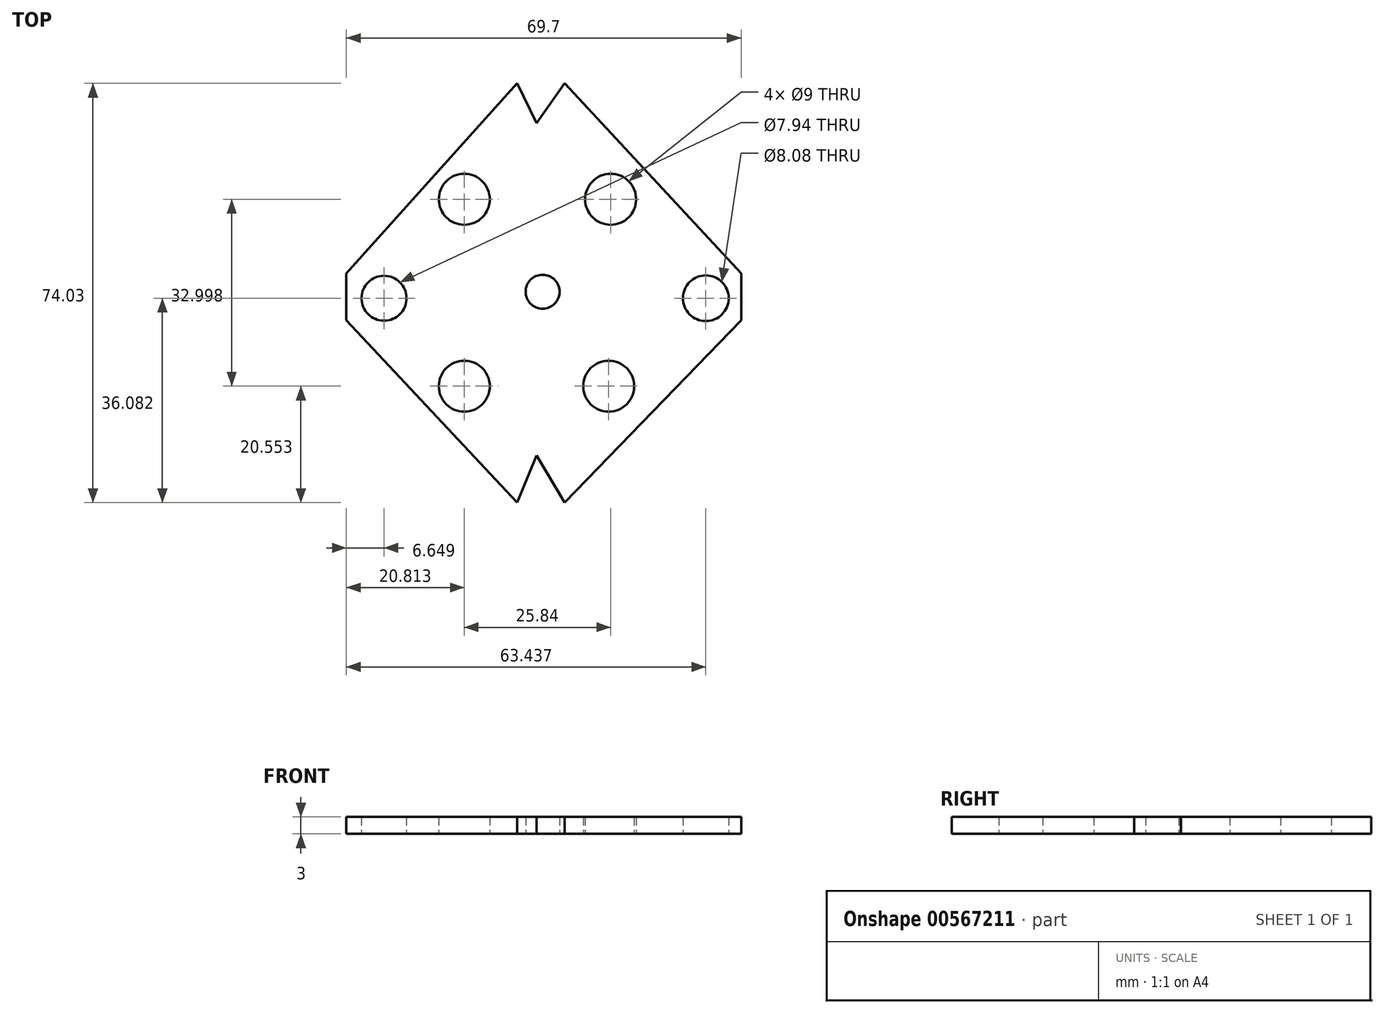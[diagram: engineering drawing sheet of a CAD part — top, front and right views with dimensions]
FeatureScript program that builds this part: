
annotation { "Feature Type Name" : "Feature", "Feature Type Description" : "" }
export const myFeature = defineFeature(function(context is Context, id is Id, definition is map)
    precondition{}
    {
        {
            var Q0;
            Q0=qCreatedBy(makeId("Top.planeOp"),FACE);
            var sketch = newSketch(context, id + "F0", { "sketchPlane" : qUnion([Q0])});
            skLineSegment(sketch, "E0.bottom", {"start": v(-2.86, 88.09) * mm, "end": v(72.14, 88.09) * mm, "construction": true});
            skLineSegment(sketch, "E0.top", {"start": v(-2.86, 13.09) * mm, "end": v(72.14, 13.09) * mm, "construction": true});
            skLineSegment(sketch, "E0.left", {"start": v(-2.86, 88.09) * mm, "end": v(-2.86, 13.09) * mm, "construction": true});
            skLineSegment(sketch, "E0.right", {"start": v(72.14, 88.09) * mm, "end": v(72.14, 13.09) * mm, "construction": true});
            skLineSegment(sketch, "E1", {"start": v(72.14, 88.09) * mm, "end": v(-2.86, 13.09) * mm, "construction": true});
            skCircle(sketch, "E2", {"center": v(34.64, 50.59) * mm, "radius": 3 * mm});
            skCircle(sketch, "E3", {"center": v(34.64, 50.59) * mm, "radius": 37.5 * mm});
            skLineSegment(sketch, "E4", {"start": v(30.12, 87.39) * mm, "end": v(38.54, 87.39) * mm});
            skLineSegment(sketch, "E5", {"start": v(38.54, 87.39) * mm, "end": v(33.56, 80.35) * mm});
            skLineSegment(sketch, "E6", {"start": v(33.56, 80.35) * mm, "end": v(30.12, 87.39) * mm});
            skLineSegment(sketch, "E7", {"start": v(30.12, 13.36) * mm, "end": v(38.54, 13.36) * mm});
            skLineSegment(sketch, "E8", {"start": v(38.54, 13.36) * mm, "end": v(33.56, 21.68) * mm});
            skLineSegment(sketch, "E9", {"start": v(33.56, 21.68) * mm, "end": v(30.12, 13.36) * mm});
            skLineSegment(sketch, "E10", {"start": v(30.12, 87.39) * mm, "end": v(30.12, 13.36) * mm});
            skLineSegment(sketch, "E11", {"start": v(38.54, 13.36) * mm, "end": v(38.54, 87.39) * mm});
            skLineSegment(sketch, "E12", {"start": v(30.12, 87.39) * mm, "end": v(0, 53.83) * mm});
            skLineSegment(sketch, "E13", {"start": v(0, 53.83) * mm, "end": v(0, 45.56) * mm});
            skLineSegment(sketch, "E14", {"start": v(0, 45.56) * mm, "end": v(30.12, 13.36) * mm});
            skLineSegment(sketch, "E15", {"start": v(38.54, 13.36) * mm, "end": v(69.7, 45.56) * mm});
            skLineSegment(sketch, "E16", {"start": v(69.7, 45.56) * mm, "end": v(69.7, 53.83) * mm});
            skLineSegment(sketch, "E17", {"start": v(69.7, 53.83) * mm, "end": v(38.54, 87.39) * mm});
            skLineSegment(sketch, "E18", {"start": v(0, 53.83) * mm, "end": v(30.12, 60.64) * mm});
            skLineSegment(sketch, "E19", {"start": v(30.12, 60.64) * mm, "end": v(38.54, 60.64) * mm});
            skLineSegment(sketch, "E20", {"start": v(38.54, 60.64) * mm, "end": v(69.7, 53.83) * mm});
            skLineSegment(sketch, "E21", {"start": v(69.7, 45.56) * mm, "end": v(38.54, 39.44) * mm});
            skLineSegment(sketch, "E22", {"start": v(38.54, 39.44) * mm, "end": v(30.12, 39.44) * mm});
            skLineSegment(sketch, "E23", {"start": v(30.12, 39.44) * mm, "end": v(0, 45.56) * mm});
            skCircle(sketch, "E24", {"center": v(20.81, 66.91) * mm, "radius": 4.5 * mm});
            skCircle(sketch, "E25", {"center": v(46.65, 66.91) * mm, "radius": 4.5 * mm});
            skCircle(sketch, "E26", {"center": v(20.81, 33.91) * mm, "radius": 4.5 * mm});
            skCircle(sketch, "E27", {"center": v(46.3, 33.91) * mm, "radius": 4.5 * mm});
            skCircle(sketch, "E28", {"center": v(6.65, 49.44) * mm, "radius": 3.97 * mm});
            skCircle(sketch, "E29", {"center": v(63.44, 49.44) * mm, "radius": 4.04 * mm});
            skSolve(sketch);
        }
        {
            var Q0;
            {var subQ0=sQuery(id+"F0.wireOp",EDGE,"E14");Q0=makeQuery(id+"F0.imprint","IMPRINT",FACE,{"disambiguationData":[TD([[makeQuery(id+"F0.imprint","IMPRINT",EDGE,{"derivedFrom":subQ0}),1.0]])]});}
            var Q1;
            Q1=makeQuery(id+"F0.imprint","IMPRINT",FACE,{"disambiguationData":[TD([[makeQuery(id+"F0.imprint","IMPRINT",EDGE,{"derivedFrom":sQuery(id+"F0.wireOp",EDGE,"E13")}),1.0]])]});
            var Q2;
            {var subQ0=sQuery(id+"F0.wireOp",EDGE,"E12");Q2=makeQuery(id+"F0.imprint","IMPRINT",FACE,{"disambiguationData":[TD([[makeQuery(id+"F0.imprint","IMPRINT",EDGE,{"derivedFrom":subQ0}),1.0]])]});}
            extrude(context, id + "F1", {"entities" : qUnion([Q0, Q1, Q2]), "depth" : 3 * mm, "offsetDistance" : 25 * mm});
        }
        {
            var Q0;
            {var subQ2=sQuery(id+"F0.wireOp",EDGE,"E5");Q0=makeQuery(id+"F0.imprint","IMPRINT",FACE,{"disambiguationData":[TD([[makeQuery(id+"F0.imprint","IMPRINT",EDGE,{"derivedFrom":subQ2}),1.0]])]});}
            var Q1;
            Q1=makeQuery(id+"F0.imprint","IMPRINT",FACE,{"disambiguationData":[TD([[makeQuery(id+"F0.imprint","IMPRINT",EDGE,{"derivedFrom":sQuery(id+"F0.wireOp",EDGE,"E2")}),-1.0]])]});
            var Q2;
            {var subQ5=sQuery(id+"F0.wireOp",EDGE,"E8");Q2=makeQuery(id+"F0.imprint","IMPRINT",FACE,{"disambiguationData":[TD([[makeQuery(id+"F0.imprint","IMPRINT",EDGE,{"derivedFrom":subQ5}),-1.0]])]});}
            extrude(context, id + "F2", {"entities" : qUnion([Q0, Q1, Q2]), "operationType" : NewBodyOperationType.ADD, "depth" : 3 * mm, "offsetDistance" : 25 * mm});
        }
        {
            var Q0;
            {var subQ0=sQuery(id+"F0.wireOp",EDGE,"E15");Q0=makeQuery(id+"F0.imprint","IMPRINT",FACE,{"disambiguationData":[TD([[makeQuery(id+"F0.imprint","IMPRINT",EDGE,{"derivedFrom":subQ0}),1.0]])]});}
            var Q1;
            {var subQ0=sQuery(id+"F0.wireOp",EDGE,"E17");Q1=makeQuery(id+"F0.imprint","IMPRINT",FACE,{"disambiguationData":[TD([[makeQuery(id+"F0.imprint","IMPRINT",EDGE,{"derivedFrom":subQ0}),1.0]])]});}
            var Q2;
            Q2=makeQuery(id+"F0.imprint","IMPRINT",FACE,{"disambiguationData":[TD([[makeQuery(id+"F0.imprint","IMPRINT",EDGE,{"derivedFrom":sQuery(id+"F0.wireOp",EDGE,"E16")}),1.0]])]});
            extrude(context, id + "F3", {"entities" : qUnion([Q0, Q1, Q2]), "operationType" : NewBodyOperationType.ADD, "depth" : 3 * mm, "offsetDistance" : 25 * mm});
        }
    });
